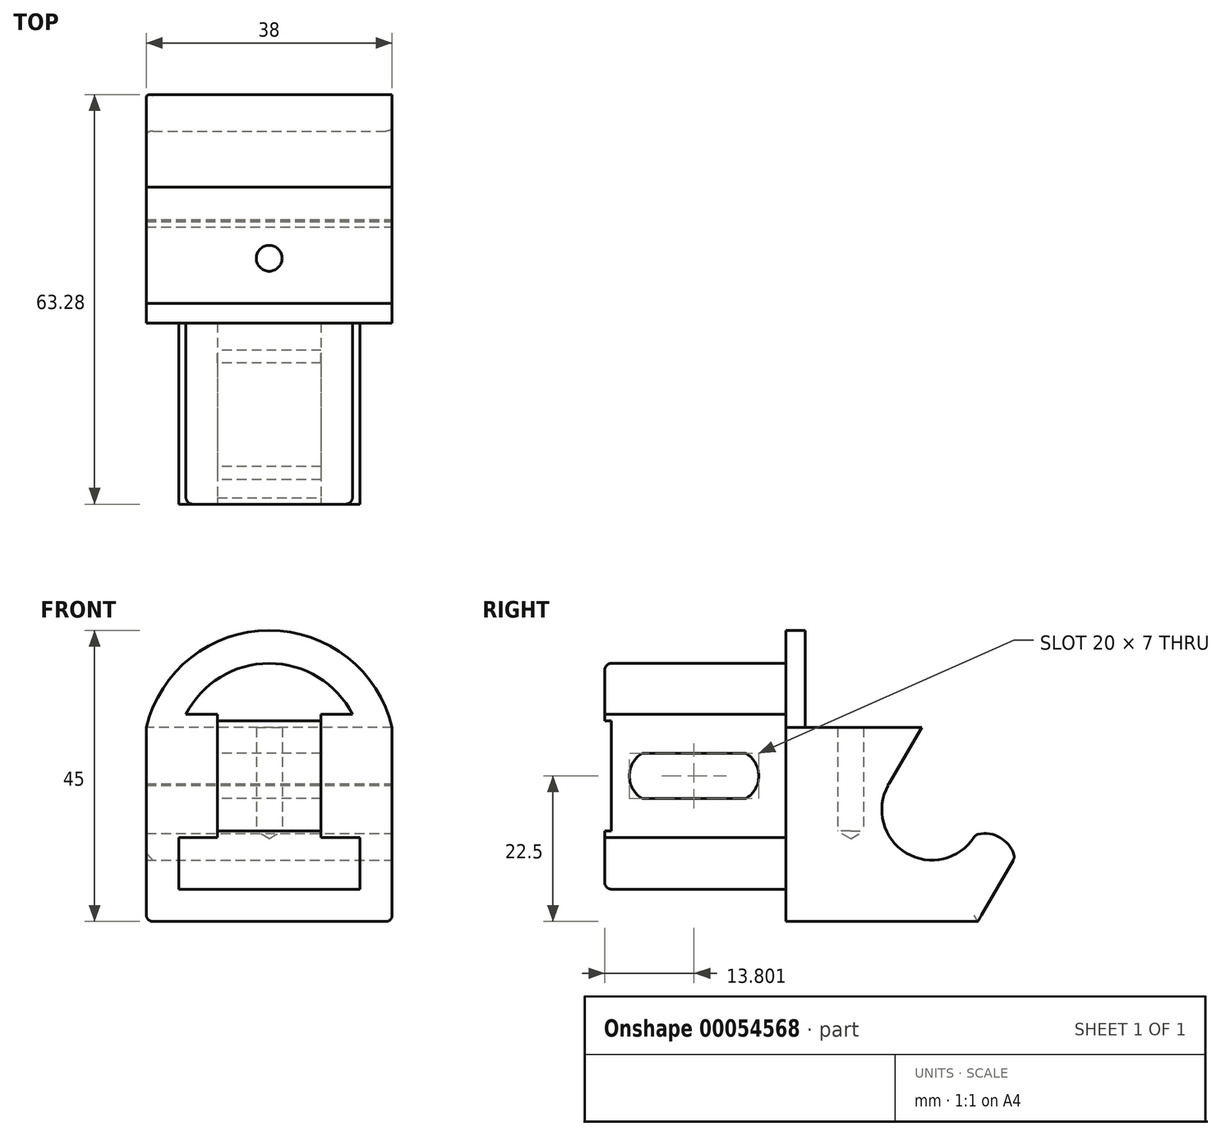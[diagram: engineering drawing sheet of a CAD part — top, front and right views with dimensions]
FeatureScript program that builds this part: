
annotation { "Feature Type Name" : "Feature", "Feature Type Description" : "" }
export const myFeature = defineFeature(function(context is Context, id is Id, definition is map)
    precondition{}
    {
        {
            var Q0;
            Q0=qCreatedBy(makeId("Front.planeOp"),FACE);
            var sketch = newSketch(context, id + "F19", { "sketchPlane" : qUnion([Q0]), "disableImprinting" : false});
            skLineSegment(sketch, "E0.bottom", {"start": v(38, 0) * mm, "end": v(0, 0) * mm});
            skLineSegment(sketch, "E0.top", {"start": v(38, 30) * mm, "end": v(0, 30) * mm});
            skLineSegment(sketch, "E0.left", {"start": v(38, 30) * mm, "end": v(38, 0) * mm});
            skLineSegment(sketch, "E0.right", {"start": v(0, 30) * mm, "end": v(0, 0) * mm});
            skArc(sketch, "E1", {"start": v(38, 30) * mm, "mid": v(19, 45) * mm, "end": v(0, 30) * mm});
            skSolve(sketch);
        }
        {
            var Q0;
            Q0=qSketchRegion(id+"F19",true);
            extrude(context, id + "F0", {"entities" : qUnion([Q0]), "oppositeDirection" : true, "depth" : 40 * mm});
        }
        {
            var Q0;
            Q0=makeQuery(id+"F19.imprint","IMPRINT",FACE,{"disambiguationData":[TD([[makeQuery(id+"F19.imprint","IMPRINT",EDGE,{"derivedFrom":sQuery(id+"F19.wireOp",EDGE,"E0.bottom")}),-1.0]])]});
            var sketch = newSketch(context, id + "F1", { "sketchPlane" : qUnion([Q0]), "disableImprinting" : false});
            skLineSegment(sketch, "E2.bottom", {"start": v(5, 5) * mm, "end": v(33, 5) * mm});
            skLineSegment(sketch, "E2.top", {"start": v(5, 29) * mm, "end": v(33, 29) * mm});
            skLineSegment(sketch, "E2.left", {"start": v(5, 5) * mm, "end": v(5, 29) * mm});
            skLineSegment(sketch, "E2.right", {"start": v(33, 5) * mm, "end": v(33, 29) * mm});
            skPoint(sketch, "E3", {"position": v(19, 25.47) * mm});
            skArc(sketch, "E4", {"start": v(5, 29) * mm, "mid": v(19, 39.9) * mm, "end": v(33, 29) * mm});
            skSolve(sketch);
        }
        {
            var Q0;
            Q0=qSketchRegion(id+"F1",true);
            extrude(context, id + "F2", {"entities" : qUnion([Q0]), "operationType" : NewBodyOperationType.ADD, "depth" : 28 * mm});
        }
        {
            var Q0;
            Q0=makeQuery(id+"F2.opExtrude","CAP_FACE",FACE,{"disambiguationData":[OSD([sQuery(id+"F1.wireOp",EDGE,"E2.bottom"),sQuery(id+"F1.wireOp",EDGE,"E2.left"),sQuery(id+"F1.wireOp",EDGE,"E2.right"),sQuery(id+"F1.wireOp",EDGE,"deeb9703-cbf5-430b-8f38-74abafe98a56")])],"isStart":false});
            var sketch = newSketch(context, id + "F3", { "sketchPlane" : qUnion([Q0]), "disableImprinting" : false});
            skLineSegment(sketch, "E5.bottom", {"start": v(5, 13) * mm, "end": v(11, 13) * mm});
            skLineSegment(sketch, "E5.top", {"start": v(5, 32) * mm, "end": v(11, 32) * mm});
            skLineSegment(sketch, "E5.left", {"start": v(5, 13) * mm, "end": v(5, 32) * mm});
            skLineSegment(sketch, "E5.right", {"start": v(11, 13) * mm, "end": v(11, 32) * mm});
            skLineSegment(sketch, "E6", {"start": v(19, 5) * mm, "end": v(19, 54.17) * mm, "construction": true});
            skPoint(sketch, "E6.endSnap0", {"position": v(19, 37) * mm});
            skLineSegment(sketch, "E7.MirrorCS", {"start": v(33, 32) * mm, "end": v(27, 32) * mm});
            skLineSegment(sketch, "E8.MirrorCS", {"start": v(33, 13) * mm, "end": v(27, 13) * mm});
            skLineSegment(sketch, "E9.MirrorCS", {"start": v(27, 13) * mm, "end": v(27, 32) * mm});
            skLineSegment(sketch, "E10.MirrorCS", {"start": v(33, 13) * mm, "end": v(33, 32) * mm});
            skSolve(sketch);
        }
        {
            var Q0;
            Q0 = qSketchRegion(id + "F3", true);
            var Q1;
            Q1=makeQuery(id+"F0.opExtrude","CAP_FACE",FACE,{"disambiguationData":[OSD([sQuery(id+"F19.wireOp",EDGE,"E0.bottom"),sQuery(id+"F19.wireOp",EDGE,"E0.left"),sQuery(id+"F19.wireOp",EDGE,"E0.right"),sQuery(id+"F19.wireOp",EDGE,"E1")])],"isStart":true});
            extrude(context, id + "F4", {"entities" : qUnion([Q0]), "operationType" : NewBodyOperationType.REMOVE, "flatOperationType" : FlatOperationType.REMOVE, "endBound" : BoundingType.UP_TO_SURFACE, "oppositeDirection" : true, "endBoundEntityFace" : qUnion([Q1]), "offsetDistance" : 25 * mm, "depth" : 25 * mm, "domain" : OperationDomain.MODEL});
        }
        {
            var Q0;
            Q0=makeQuery(id+"F2.opExtrude","CAP_FACE",FACE,{"disambiguationData":[OSD([sQuery(id+"F1.wireOp",EDGE,"E2.bottom"),sQuery(id+"F1.wireOp",EDGE,"E2.left"),sQuery(id+"F1.wireOp",EDGE,"E2.right"),sQuery(id+"F1.wireOp",EDGE,"E4")])],"isStart":false});
            var sketch = newSketch(context, id + "F5", { "sketchPlane" : qUnion([Q0])});
            skLineSegment(sketch, "E11.bottom", {"start": v(11, 14) * mm, "end": v(27, 14) * mm});
            skLineSegment(sketch, "E11.top", {"start": v(11, 31) * mm, "end": v(27, 31) * mm});
            skLineSegment(sketch, "E11.left", {"start": v(11, 14) * mm, "end": v(11, 31) * mm});
            skLineSegment(sketch, "E11.right", {"start": v(27, 14) * mm, "end": v(27, 31) * mm});
            skSolve(sketch);
        }
        {
            var Q0;
            Q0=makeQuery(id+"F5.imprint","IMPRINT",FACE,{"disambiguationData":[TD([[makeQuery(id+"F5.imprint","IMPRINT",EDGE,{"derivedFrom":sQuery(id+"F5.wireOp",EDGE,"E11.bottom")}),1.0]])]});
            extrude(context, id + "F6", {"entities" : qUnion([Q0]), "operationType" : NewBodyOperationType.REMOVE, "oppositeDirection" : true, "depth" : 1 * mm});
        }
        {
            var Q0;
            Q0=makeQuery(id+"F4.boolean.opBoolean","COPY",FACE,{"derivedFrom":makeQuery(id+"F4.opExtrude","SWEPT_FACE",FACE,{"disambiguationData":[OSD([sQuery(id+"F3.wireOp",EDGE,"E5.right")])]})});
            var sketch = newSketch(context, id + "F7", { "sketchPlane" : qUnion([Q0]), "disableImprinting" : false});
            skLineSegment(sketch, "E12.bottom", {"start": v(6.2, 26) * mm, "end": v(22.2, 26) * mm});
            skLineSegment(sketch, "E12.top", {"start": v(6.2, 19) * mm, "end": v(22.2, 19) * mm});
            skLineSegment(sketch, "E12.left", {"start": v(6.2, 26) * mm, "end": v(6.2, 19) * mm});
            skLineSegment(sketch, "E12.right", {"start": v(22.2, 26) * mm, "end": v(22.2, 19) * mm});
            skArc(sketch, "E13", {"start": v(22.2, 19) * mm, "mid": v(24.2, 22.5) * mm, "end": v(22.2, 26) * mm});
            skArc(sketch, "E14", {"start": v(6.2, 26) * mm, "mid": v(4.2, 22.5) * mm, "end": v(6.2, 19) * mm});
            skPoint(sketch, "E15", {"position": v(27, 22.5) * mm});
            skSolve(sketch);
        }
        {
            var Q0;
            Q0=qSketchRegion(id+"F7",true);
            var Q1;
            Q1=makeQuery(id+"F4.boolean.opBoolean","COPY",FACE,{"derivedFrom":makeQuery(id+"F4.opExtrude","SWEPT_FACE",FACE,{"disambiguationData":[OSD([sQuery(id+"F3.wireOp",EDGE,"E9.MirrorCS")])]})});
            extrude(context, id + "F8", {"entities" : qUnion([Q0]), "operationType" : NewBodyOperationType.REMOVE, "endBound" : BoundingType.UP_TO_SURFACE, "oppositeDirection" : true, "endBoundEntityFace" : qUnion([Q1]), "depth" : 25 * mm});
        }
        {
            var Q0;
            Q0=makeQuery(id+"F0.opExtrude","CAP_FACE",FACE,{"disambiguationData":[OSD([sQuery(id+"F19.wireOp",EDGE,"E0.bottom"),sQuery(id+"F19.wireOp",EDGE,"E0.left"),sQuery(id+"F19.wireOp",EDGE,"E0.right"),sQuery(id+"F19.wireOp",EDGE,"E1")])],"isStart":false});
            var sketch = newSketch(context, id + "F9", { "sketchPlane" : qUnion([Q0])});
            skArc(sketch, "E16", {"start": v(0, 30) * mm, "mid": v(-19, 45) * mm, "end": v(-38, 30) * mm});
            skLineSegment(sketch, "E17", {"start": v(-38, 30) * mm, "end": v(0, 30) * mm});
            skSolve(sketch);
        }
        {
            var Q0;
            Q0=qSketchRegion(id+"F9",true);
            extrude(context, id + "F10", {"entities" : qUnion([Q0]), "operationType" : NewBodyOperationType.REMOVE, "oppositeDirection" : true, "depth" : 37 * mm});
        }
        {
            var Q0;
            Q0=makeQuery(id+"F10.boolean.opBoolean","COPY",FACE,{"derivedFrom":makeQuery(id+"F10.opExtrude","SWEPT_FACE",FACE,{"disambiguationData":[OSD([sQuery(id+"F9.wireOp",EDGE,"E17")])]})});
            var sketch = newSketch(context, id + "F11", { "sketchPlane" : qUnion([Q0])});
            skPoint(sketch, "E18", {"position": v(19, 40) * mm});
            skLineSegment(sketch, "E19", {"start": v(19, 66.38) * mm, "end": v(19, -49.4) * mm, "construction": true});
            skPoint(sketch, "E19.endSnap0", {"position": v(19, 3) * mm});
            skPoint(sketch, "E20", {"position": v(19, 10) * mm});
            skSolve(sketch);
        }
        {
            var Q0;
            Q0=sQuery(id+"F11.wireOp",VERTEX,"E20");
            var Q1;
            Q1=makeQuery(id+"F0.opExtrude","SWEPT_BODY",BODY,{"disambiguationData":[OSD([sQuery(id+"F19.wireOp",EDGE,"E0.bottom"),sQuery(id+"F19.wireOp",EDGE,"E0.left"),sQuery(id+"F19.wireOp",EDGE,"E0.right"),sQuery(id+"F19.wireOp",EDGE,"E1")])]});
            hole(context, id + "F12", {"style" : HoleStyle.SIMPLE, "holeDiameter" : 4 * mm, "endStyle" : HoleEndStyle.BLIND, "holeDepth" : 16 * mm, "locations" : qUnion([Q0]), "scope" : qUnion([Q1])});
        }
        {
            var Q0;
            Q0=makeQuery(id+"F0.opExtrude","SWEPT_FACE",FACE,{"disambiguationData":[OSD([sQuery(id+"F19.wireOp",EDGE,"E0.left")])]});
            var sketch = newSketch(context, id + "F13", { "sketchPlane" : qUnion([Q0])});
            skLineSegment(sketch, "E21", {"start": v(15.87, 21.11) * mm, "end": v(23.37, 34.1) * mm});
            skLineSegment(sketch, "E22", {"start": v(23.37, 34.1) * mm, "end": v(36.8, 26.35) * mm});
            skLineSegment(sketch, "E23", {"start": v(36.8, 26.35) * mm, "end": v(29.3, 13.36) * mm});
            skLineSegment(sketch, "E24", {"start": v(29.3, 13.36) * mm, "end": v(15.87, 21.11) * mm});
            skArc(sketch, "E25", {"start": v(36.8, 26.35) * mm, "mid": v(33.95, 36.94) * mm, "end": v(23.37, 34.1) * mm});
            skArc(sketch, "E26", {"start": v(15.87, 21.11) * mm, "mid": v(18.7, 10.52) * mm, "end": v(29.3, 13.36) * mm});
            skPoint(sketch, "E27", {"position": v(21, 30) * mm});
            skSolve(sketch);
        }
        {
            var Q0;
            Q0=qSketchRegion(id+"F13",true);
            extrude(context, id + "F14", {"entities" : qUnion([Q0]), "operationType" : NewBodyOperationType.REMOVE, "endBound" : BoundingType.UP_TO_NEXT, "oppositeDirection" : true, "depth" : 25 * mm});
        }
        {
            var Q0;
            Q0=makeQuery(id+"F0.opExtrude","SWEPT_FACE",FACE,{"disambiguationData":[OSD([sQuery(id+"F19.wireOp",EDGE,"E0.left")])]});
            var sketch = newSketch(context, id + "F15", { "sketchPlane" : qUnion([Q0])});
            skLineSegment(sketch, "E28", {"start": v(50.7, 0) * mm, "end": v(29.66, 0) * mm});
            skLineSegment(sketch, "E29", {"start": v(50.7, 0) * mm, "end": v(40.66, 34.36) * mm});
            skLineSegment(sketch, "E30", {"start": v(40.66, 34.36) * mm, "end": v(15.67, 21.12) * mm});
            skPoint(sketch, "E31", {"position": v(29.3, 13.36) * mm});
            skLineSegment(sketch, "E32", {"start": v(29.66, 0) * mm, "end": v(35.35, 9.86) * mm});
            skLineSegment(sketch, "E33", {"start": v(15.67, 21.12) * mm, "end": v(29.3, 13.36) * mm});
            skLineSegment(sketch, "E34", {"start": v(35.35, 9.86) * mm, "end": v(35.35, 9.86) * mm});
            skArc(sketch, "E35", {"start": v(35.35, 9.86) * mm, "mid": v(33.1, 12.97) * mm, "end": v(29.3, 13.36) * mm});
            skLineSegment(sketch, "E36", {"start": v(29.3, 13.36) * mm, "end": v(35.35, 9.86) * mm, "construction": true});
            skSolve(sketch);
        }
        {
            var Q0;
            Q0=qSketchRegion(id+"F15",true);
            extrude(context, id + "F16", {"entities" : qUnion([Q0]), "operationType" : NewBodyOperationType.REMOVE, "endBound" : BoundingType.THROUGH_ALL, "oppositeDirection" : true, "depth" : 25 * mm});
        }
        {
            var Q0;
            Q0=makeQuery(id+"F2.opExtrude","CAP_EDGE",EDGE,{"disambiguationData":[OSD([sQuery(id+"F1.wireOp",EDGE,"E4")])],"isStart":false});
            var Q1;
            Q1=makeQuery(id+"F4.boolean.opBoolean","COPY",EDGE,{"derivedFrom":makeQuery(id+"F4.opExtrude","CAP_EDGE",EDGE,{"disambiguationData":[OSD([sQuery(id+"F3.wireOp",EDGE,"E5.top")])],"isStart":true})});
            var Q2;
            Q2=makeQuery(id+"F4.boolean.opBoolean","COPY",EDGE,{"derivedFrom":makeQuery(id+"F4.opExtrude","CAP_EDGE",EDGE,{"disambiguationData":[OSD([sQuery(id+"F3.wireOp",EDGE,"E7.MirrorCS")])],"isStart":true})});
            fillet(context, id + "F17", {"entities" : qUnion([Q0, Q1, Q2]), "radius" : 1 * mm, "tangentPropagation" : true, "allowEdgeOverflow" : false});
        }
        {
            var Q0;
            Q0=makeQuery(id+"F0.opExtrude","SWEPT_EDGE",EDGE,{"disambiguationData":[OSD([sQuery(id+"F19.wireOp",EDGE,"E0.bottom"),sQuery(id+"F19.wireOp",EDGE,"E0.right")])]});
            var Q1;
            Q1=makeQuery(id+"F0.opExtrude","SWEPT_EDGE",EDGE,{"disambiguationData":[OSD([sQuery(id+"F19.wireOp",EDGE,"E0.bottom"),sQuery(id+"F19.wireOp",EDGE,"E0.left")])]});
            var Q2;
            Q2=makeQuery(id+"F16.boolean.opBoolean","COPY",EDGE,{"derivedFrom":makeQuery(id+"F16.opExtrude","SWEPT_EDGE",EDGE,{"disambiguationData":[OSD([sQuery(id+"F19.wireOp",EDGE,"E0.bottom"),sQuery(id+"F19.wireOp",EDGE,"E0.left"),sQuery(id+"F15.wireOp",EDGE,"E28"),sQuery(id+"F15.wireOp",EDGE,"E32")])]})});
            var Q3;
            Q3=makeQuery(id+"F16.boolean.opBoolean","COPY",EDGE,{"derivedFrom":makeQuery(id+"F16.opExtrude","CAP_EDGE",EDGE,{"disambiguationData":[OSD([sQuery(id+"F15.wireOp",EDGE,"E32")])],"isStart":true})});
            var Q4;
            Q4=makeQuery(id+"F16.boolean.opBoolean","INTERSECT",EDGE,{"derivedFrom":[makeQuery(id+"F0.opExtrude","SWEPT_FACE",FACE,{"disambiguationData":[OSD([sQuery(id+"F19.wireOp",EDGE,"E0.right")])]}),makeQuery(id+"F16.opExtrude","SWEPT_FACE",FACE,{"disambiguationData":[OSD([sQuery(id+"F15.wireOp",EDGE,"E32")])]})]});
            var Q5;
            Q5=makeQuery(id+"F4.boolean.opBoolean","COPY",EDGE,{"derivedFrom":makeQuery(id+"F4.opExtrude","CAP_EDGE",EDGE,{"disambiguationData":[OSD([sQuery(id+"F3.wireOp",EDGE,"E8.MirrorCS")])],"isStart":true})});
            var Q6;
            Q6=makeQuery(id+"F4.boolean.opBoolean","COPY",EDGE,{"derivedFrom":makeQuery(id+"F4.opExtrude","CAP_EDGE",EDGE,{"disambiguationData":[OSD([sQuery(id+"F3.wireOp",EDGE,"E5.bottom")])],"isStart":true})});
            var Q7;
            Q7=makeQuery(id+"F2.opExtrude","CAP_EDGE",EDGE,{"disambiguationData":[OSD([sQuery(id+"F1.wireOp",EDGE,"E2.bottom")])],"isStart":false});
            var Q8;
            Q8=makeQuery(id+"F16.boolean.opBoolean","COPY",EDGE,{"derivedFrom":makeQuery(id+"F16.opExtrude","SWEPT_EDGE",EDGE,{"disambiguationData":[OSD([sQuery(id+"F15.wireOp",EDGE,"E32"),sQuery(id+"F15.wireOp",EDGE,"E35")])]})});
            var Q9;
            {var subQ0=sQuery(id+"F13.wireOp",EDGE,"E26");var subQ1=sQuery(id+"F13.wireOp",EDGE,"E23");Q9=makeQuery(id+"F16.boolean.opBoolean","MERGE",EDGE,{"derivedFrom":[makeQuery(id+"F14.boolean.opBoolean","COPY",EDGE,{"derivedFrom":makeQuery(id+"F14.opExtrude","SWEPT_EDGE",EDGE,{"disambiguationData":[OSD([subQ1,sQuery(id+"F13.wireOp",EDGE,"E24"),subQ0])]})}),makeQuery(id+"F16.opExtrude","SWEPT_EDGE",EDGE,{"disambiguationData":[OSD([subQ1,subQ0,sQuery(id+"F15.wireOp",EDGE,"E33"),sQuery(id+"F15.wireOp",EDGE,"E35")])]})]});}
            fillet(context, id + "F18", {"entities" : qUnion([Q0, Q1, Q2, Q3, Q4, Q5, Q6, Q7, Q8, Q9]), "radius" : 1 * mm, "tangentPropagation" : true, "allowEdgeOverflow" : false});
        }
    });
